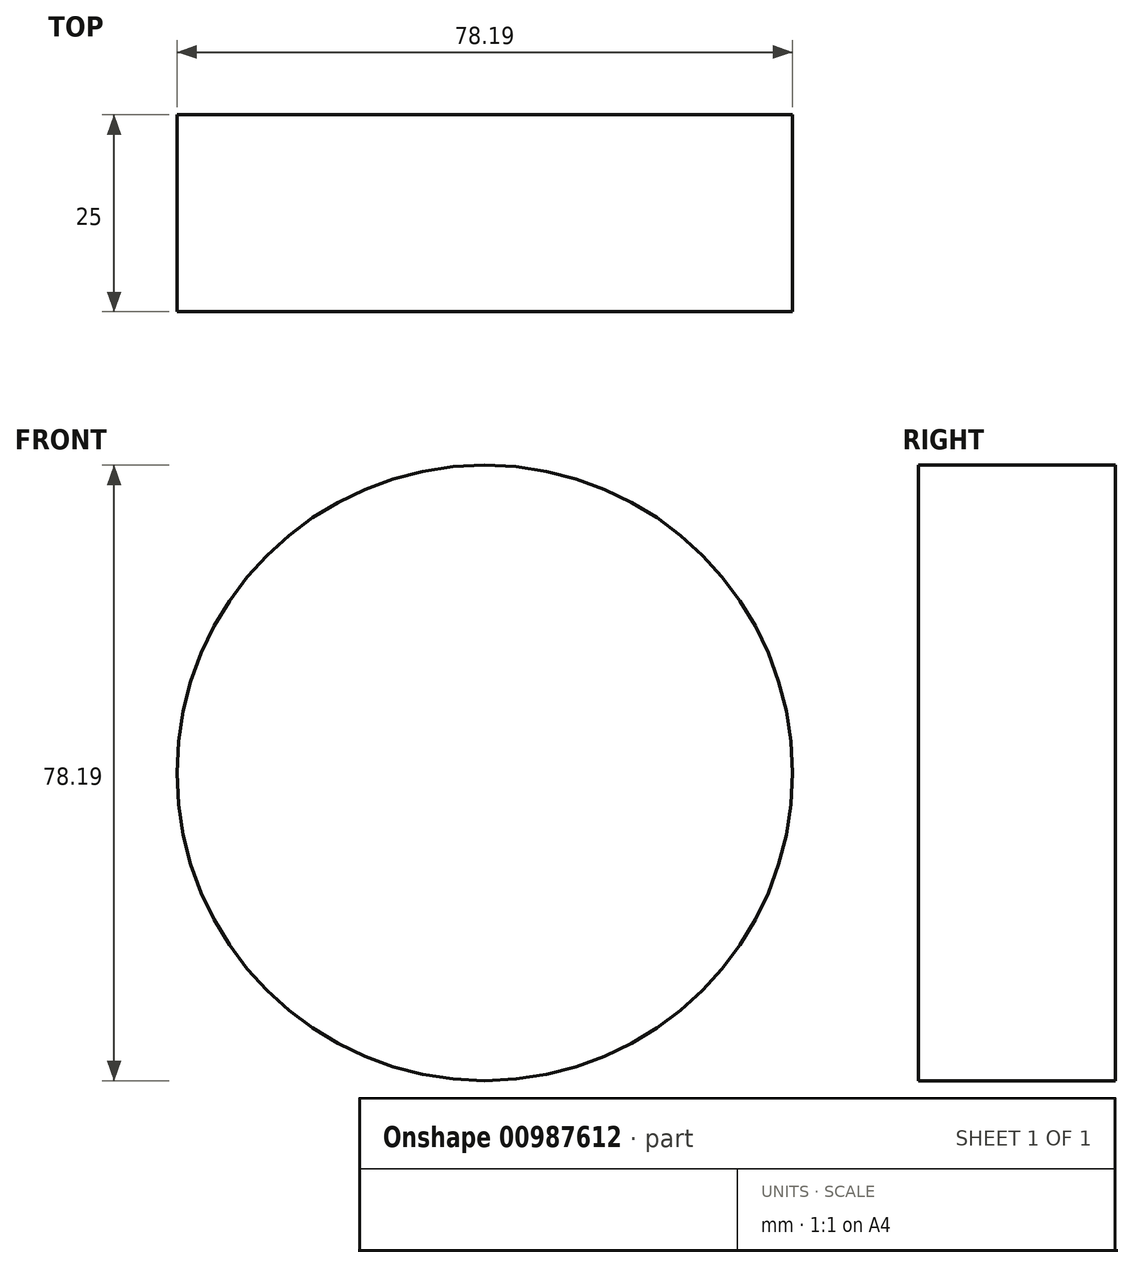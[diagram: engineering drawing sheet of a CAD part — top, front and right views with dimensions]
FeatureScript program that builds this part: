
annotation { "Feature Type Name" : "Feature", "Feature Type Description" : "" }
export const myFeature = defineFeature(function(context is Context, id is Id, definition is map)
    precondition{}
    {
        {
            var Q0;
            Q0=qCreatedBy(makeId("Front.planeOp"),FACE);
            var sketch = newSketch(context, id + "F0", { "sketchPlane" : qUnion([Q0])});
            skCircle(sketch, "E0", {"center": v(-32.75, 19.53) * mm, "radius": 39.1 * mm});
            skSolve(sketch);
        }
        {
            var Q0;
            Q0 = qSketchRegion(id + "F0", true);
            extrude(context, id + "F1", {"entities" : qUnion([Q0]), "depth" : 25 * mm, "offsetDistance" : 25 * mm});
        }
    });
